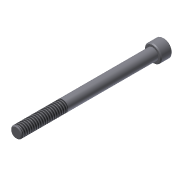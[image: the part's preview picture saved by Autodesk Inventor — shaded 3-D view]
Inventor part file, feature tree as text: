
AUTODESK INVENTOR PART (.ipt)
format: ipt  version: 2011 (Build 150239000, 239)  size: 104,960 bytes
history: native  units: in
note: dims shown in document units (in); Inventor stores cm internally (conversion verified against a paired STEP export)
features: extrude x3, sketch x3, chamfer x1, thread x1
ambient origin geometry x8: Origin, YZ Plane, XZ Plane, XY Plane, X Axis, Y Axis, Z Axis, Center Point
bodies: Solid1 (feature_tree)
feature tree (8):
  extrude  "Extrusion1"  Depth=3.0in TaperAngle=0.0deg
  extrude  "Extrusion2"  Depth=0.25in TaperAngle=0.0deg
  extrude  "Extrusion3"  Depth=0.125in TaperAngle=0.0deg
  chamfer  "Chamfer1"  Distance=0.02in Angle=45.0deg
  thread  "Thread1"  [1 undecoded]
  sketch  "Sketch1"  dims[d0=0.25in d1=3.0in d2=0.0in]
  sketch  "Sketch2"  dims[d3=0.375in d4=0.25in d5=0.0in]
  sketch  "Sketch3"  dims[d6=0.1875in d7=0.125in d8=0.0in d9=0.02in d10=0.125in d11=45.0deg d12=1.0in d13=0.0in]
note: 1 required parameter value undecoded (feature->parameter linkage not recoverable at this tier; creation-order binding heuristic only, values carry confidence <= 0.55)
